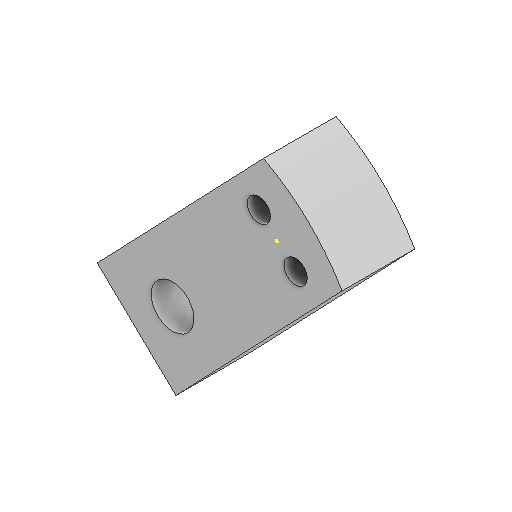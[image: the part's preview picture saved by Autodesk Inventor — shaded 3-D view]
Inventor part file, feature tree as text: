
AUTODESK INVENTOR PART (.ipt)
format: ipt  version: 2022 (Build 260153000, 153)  size: 106,496 bytes
history: native  units: mm
features: other x4, sketch x3, reference x3, extrude x1
ambient origin geometry x8: Origin, YZ Plane, XZ Plane, XY Plane, X Axis, Y Axis, Z Axis, Center Point
bodies: Volumenkörper1 (feature_tree)
feature tree (11):
  extrude  "Extrusion1"  Depth=5.9mm
  sketch  "Skizze2"  dims[d2=3.2mm]
  sketch  "Skizze3"  dims[d3=3.2mm d4=10.0mm d5=0.0mm]
  sketch  "Skizze1"  dims[d0=23.0mm d1=5.9mm]
  reference  "Referenz1"
  reference  "Referenz2"
  reference  "Referenz3"
  other  "Assembly_Matchboxscope_injectionmolded_holo.iam"
  other  "IM_Matchboxscope_Laserholder:1"
  other  "00_laserpointer_red:2"
  other  "00_mk8_nozzle_0.4STEP:1"
